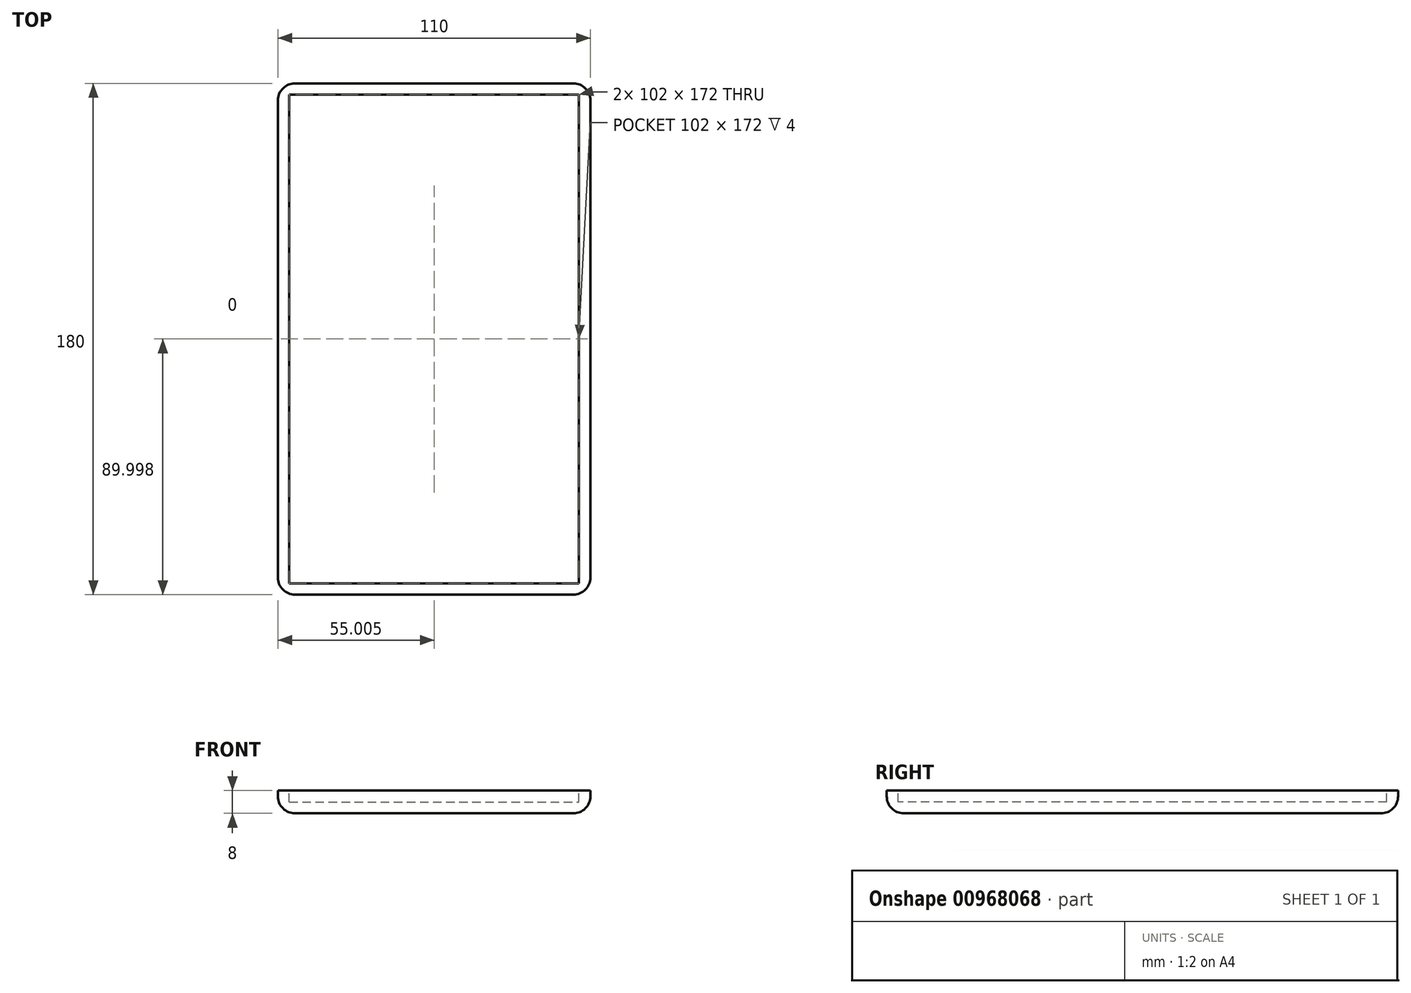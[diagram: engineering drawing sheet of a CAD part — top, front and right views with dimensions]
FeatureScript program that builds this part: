
annotation { "Feature Type Name" : "Feature", "Feature Type Description" : "" }
export const myFeature = defineFeature(function(context is Context, id is Id, definition is map)
    precondition{}
    {
        {
            var Q0;
            Q0=qCreatedBy(makeId("Top.planeOp"),FACE);
            var sketch = newSketch(context, id + "F0", { "sketchPlane" : qUnion([Q0])});
            skLineSegment(sketch, "E0.bottom", {"start": v(-88.89, -82.4) * mm, "end": v(21.11, -82.4) * mm});
            skLineSegment(sketch, "E0.top", {"start": v(-88.89, 97.6) * mm, "end": v(21.11, 97.6) * mm});
            skLineSegment(sketch, "E0.left", {"start": v(-88.89, -82.4) * mm, "end": v(-88.89, 97.6) * mm});
            skLineSegment(sketch, "E0.right", {"start": v(21.11, -82.4) * mm, "end": v(21.11, 97.6) * mm});
            skSolve(sketch);
        }
        {
            var Q0;
            Q0=makeQuery(id+"F0.imprint","IMPRINT",FACE,{"disambiguationData":[TD([[makeQuery(id+"F0.imprint","IMPRINT",EDGE,{"derivedFrom":sQuery(id+"F0.wireOp",EDGE,"E0.bottom")}),1.0]])]});
            extrude(context, id + "F1", {"entities" : qUnion([Q0]), "depth" : 8 * mm, "offsetDistance" : 25 * mm});
        }
        {
            var Q0;
            Q0=makeQuery(id+"F1.opExtrude","CAP_FACE",FACE,{"disambiguationData":[OSD([sQuery(id+"F0.wireOp",EDGE,"E0.bottom"),sQuery(id+"F0.wireOp",EDGE,"E0.top"),sQuery(id+"F0.wireOp",EDGE,"E0.left"),sQuery(id+"F0.wireOp",EDGE,"E0.right")])],"isStart":false});
            var sketch = newSketch(context, id + "F2", { "sketchPlane" : qUnion([Q0])});
            skLineSegment(sketch, "E1.bottom", {"start": v(-84.89, 93.6) * mm, "end": v(17.11, 93.6) * mm});
            skLineSegment(sketch, "E1.top", {"start": v(-84.89, -78.4) * mm, "end": v(17.11, -78.4) * mm});
            skLineSegment(sketch, "E1.left", {"start": v(-84.89, 93.6) * mm, "end": v(-84.89, -78.4) * mm});
            skLineSegment(sketch, "E1.right", {"start": v(17.11, 93.6) * mm, "end": v(17.11, -78.4) * mm});
            skSolve(sketch);
        }
        {
            var Q0;
            Q0=makeQuery(id+"F2.imprint","IMPRINT",FACE,{"disambiguationData":[TD([[makeQuery(id+"F2.imprint","IMPRINT",EDGE,{"derivedFrom":sQuery(id+"F2.wireOp",EDGE,"E1.bottom")}),-1.0]])]});
            extrude(context, id + "F3", {"entities" : qUnion([Q0]), "operationType" : NewBodyOperationType.REMOVE, "oppositeDirection" : true, "depth" : 4 * mm, "offsetDistance" : 25 * mm});
        }
        {
            var Q0;
            Q0=makeQuery(id+"F1.opExtrude","SWEPT_EDGE",EDGE,{"disambiguationData":[OSD([sQuery(id+"F0.wireOp",EDGE,"E0.bottom"),sQuery(id+"F0.wireOp",EDGE,"E0.left")])]});
            var Q1;
            Q1=makeQuery(id+"F1.opExtrude","SWEPT_EDGE",EDGE,{"disambiguationData":[OSD([sQuery(id+"F0.wireOp",EDGE,"E0.bottom"),sQuery(id+"F0.wireOp",EDGE,"E0.right")])]});
            var Q2;
            Q2=makeQuery(id+"F1.opExtrude","SWEPT_EDGE",EDGE,{"disambiguationData":[OSD([sQuery(id+"F0.wireOp",EDGE,"E0.top"),sQuery(id+"F0.wireOp",EDGE,"E0.right")])]});
            var Q3;
            Q3=makeQuery(id+"F1.opExtrude","SWEPT_EDGE",EDGE,{"disambiguationData":[OSD([sQuery(id+"F0.wireOp",EDGE,"E0.top"),sQuery(id+"F0.wireOp",EDGE,"E0.left")])]});
            var Q4;
            Q4=makeQuery(id+"F1.opExtrude","CAP_EDGE",EDGE,{"disambiguationData":[OSD([sQuery(id+"F0.wireOp",EDGE,"E0.left")])],"isStart":true});
            var Q5;
            Q5=makeQuery(id+"F1.opExtrude","CAP_EDGE",EDGE,{"disambiguationData":[OSD([sQuery(id+"F0.wireOp",EDGE,"E0.top")])],"isStart":true});
            var Q6;
            Q6=makeQuery(id+"F1.opExtrude","CAP_EDGE",EDGE,{"disambiguationData":[OSD([sQuery(id+"F0.wireOp",EDGE,"E0.right")])],"isStart":true});
            var Q7;
            Q7=makeQuery(id+"F1.opExtrude","CAP_EDGE",EDGE,{"disambiguationData":[OSD([sQuery(id+"F0.wireOp",EDGE,"E0.bottom")])],"isStart":true});
            fillet(context, id + "F4", {"entities" : qUnion([Q0, Q1, Q2, Q3, Q4, Q5, Q6, Q7]), "radius" : 6 * mm, "tangentPropagation" : true, "allowEdgeOverflow" : false});
        }
    });
